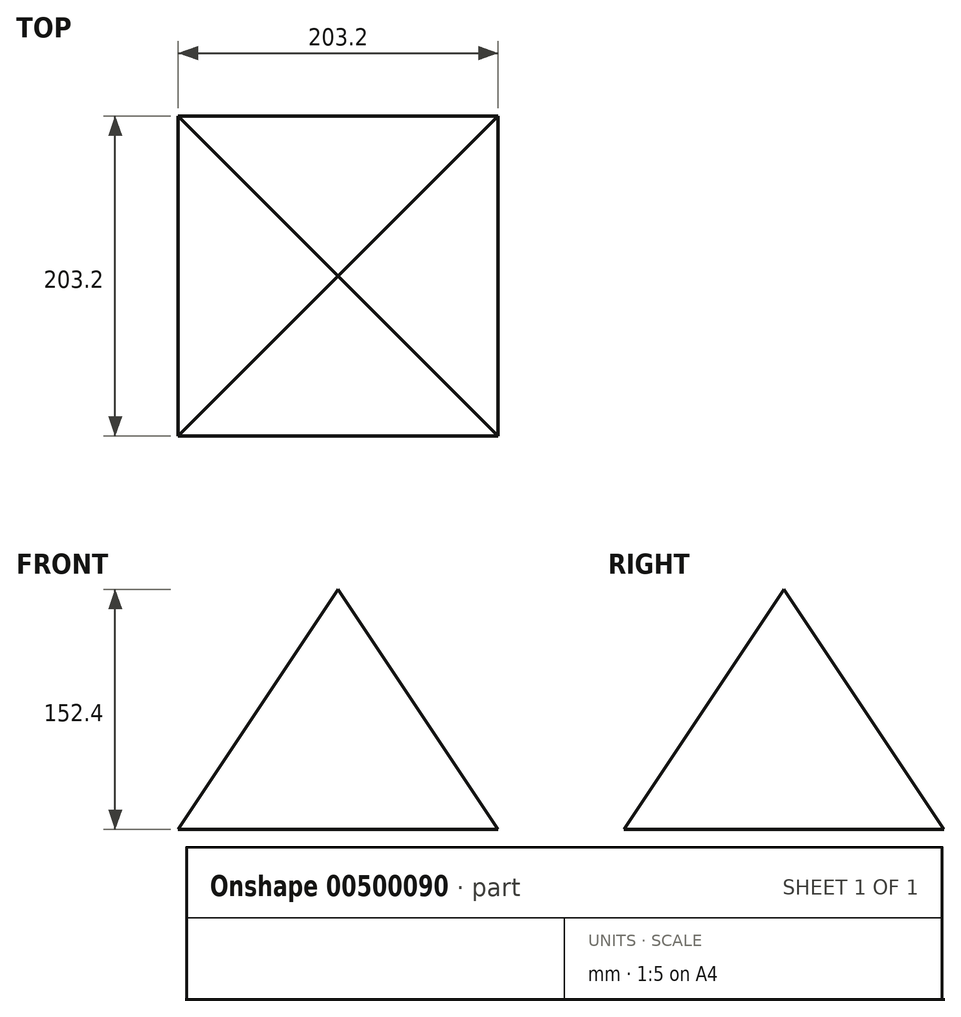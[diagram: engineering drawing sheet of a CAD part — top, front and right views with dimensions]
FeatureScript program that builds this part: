
annotation { "Feature Type Name" : "Feature", "Feature Type Description" : "" }
export const myFeature = defineFeature(function(context is Context, id is Id, definition is map)
    precondition{}
    {
        {
            var Q0;
            Q0=qCreatedBy(makeId("Top.planeOp"),FACE);
            var sketch = newSketch(context, id + "F0", { "sketchPlane" : qUnion([Q0])});
            skLineSegment(sketch, "E0.bottom", {"start": v(101.6, -101.6) * mm, "end": v(-101.6, -101.6) * mm});
            skLineSegment(sketch, "E0.top", {"start": v(101.6, 101.6) * mm, "end": v(-101.6, 101.6) * mm});
            skLineSegment(sketch, "E0.left", {"start": v(101.6, -101.6) * mm, "end": v(101.6, 101.6) * mm});
            skLineSegment(sketch, "E0.right", {"start": v(-101.6, -101.6) * mm, "end": v(-101.6, 101.6) * mm});
            skPoint(sketch, "E0.middle", {"position": v(0, 0) * mm});
            skSolve(sketch);
        }
        {
            var Q0;
            Q0=qCreatedBy(makeId("Top.planeOp"),FACE);
            cPlane(context, id + "F1", {"entities" : qUnion([Q0]), "cplaneType" : CPlaneType.OFFSET, "offset" : 152.4 * mm, "width" : 152.4 * mm, "height" : 152.4 * mm});
        }
        {
            var Q0;
            Q0=qCreatedBy(id+"F1.planeOp",FACE);
            var sketch = newSketch(context, id + "F2", { "sketchPlane" : qUnion([Q0])});
            skPoint(sketch, "E1", {"position": v(0, 0) * mm});
            skSolve(sketch);
        }
        {
            var Q0;
            Q0=makeQuery(id+"F0.imprint","IMPRINT",FACE,{"disambiguationData":[TD([[makeQuery(id+"F0.imprint","IMPRINT",EDGE,{"derivedFrom":sQuery(id+"F0.wireOp",EDGE,"E0.bottom")}),-1.0]])]});
            var Q1;
            Q1=sQuery(id+"F2.wireOp",VERTEX,"E1");
            loft(context, id + "F3", {"sheetProfilesArray" : [{ "sheetProfileEntities" : qUnion([Q0]) }, { "sheetProfileEntities" : qUnion([Q1]) }]});
        }
    });
